# Revit family: Lankateline ilman kantta
name_source: partatom
category: Casework
revit_build: Autodesk Revit 2015 (Build: 20140606_1530(x64)
units: mm (PartAtom-declared; Revit-internal decimal feet)

## types (2) — shared parameters
Depth = 255 mm  [stored 0.836614 ft]
Height = 500 mm  [stored 1.64042 ft]
Keynote = 1882N
Manufacturer = Korpinen
Model = Lankateline ilman kantta
NominalLength = 8 mm  [stored 0.0262467 ft]
URL = http://www.korpinen.com
Width = 340 mm  [stored 1.11549 ft]
large_tube_radius = 5 mm  [stored 0.0164042 ft]
small_tube_radius = 3 mm  [stored 0.00984252 ft]
zero-valued in all types: NominalDepth, NominalHeight

## per-type parameters (varying)
| type | ruostumaton teräs |
| 1882N rosteri | ruostumaton teräs |
| 1882N valkoinen | ruostumaton teräs valkoinen |

note: [stored X ft] marks values corroborated as IEEE doubles in the binary element streams (Revit-internal decimal feet)

## geometry (parser evidence)
native form markers: Sweep x3
no freeform markers — native parametric forms only
